# Revit family: HARMANN - INDUFLOW CPC
name_source: partatom
category: Mechanical Equipment
units: mm (PartAtom-declared; Revit-internal decimal feet)

## family parameters
Always vertical = No
Cut with Voids When Loaded = No
Maintain Annotation Orientation = No
OmniClass Number = 23.75.00.00
OmniClass Title = Climate Control (HVAC)
Part Type = Normal
Room Calculation Point = No
Round Connector Dimension = Use Diameter
Shared = No
Work Plane-Based = No

## types (4) — shared parameters
Autor = https://www.archispace.com
Description = Indukcyjny wentylator bytowy
G = 285 mm  [stored 0.935039 ft]
H = 15 mm  [stored 0.0492126 ft]
Ilość faz = 3
Lookup Table Name = INDUFLOW_CPC
Manufacturer = Harmann Polska Sp. z o.o.
Temperatura maksymalna Tmax = 60 °C
Wyłącznik serwisowy = AS
Zasilanie Częstotliwość Nominalna = 50 Hz
Zasilanie napięcie nominalne Unom = 400 V
d = 77 mm  [stored 0.252625 ft]
e = 15 mm  [stored 0.0492126 ft]
h = 70 mm  [stored 0.229659 ft]
zero-valued in all types: Default Elevation

## per-type parameters (varying)
- INDUFLOW CPC 500 D4: A=1446 mm  [stored 4.74409 ft]; B=273 mm  [stored 0.895669 ft]; C=870 mm  [stored 2.85433 ft]; Ciśnienie akustyczne nominalne I bieg Lpa=76.0 dB(A); Ciśnienie akustyczne nominalne II bieg Lpa=-; E=950 mm  [stored 3.1168 ft]; F=243 mm  [stored 0.797244 ft]; K=914 mm  [stored 2.99869 ft]; Masa=56.00 kg; N1=1 mm; Numer artykułu=15957800; Obroty maksymalne I bieg nmax=0.000 RPM; Obroty maksymalne II bieg nmax=1450.000 RPM; Powietrze Przepływ Maksymalny I Qmax=0 m³/h; Powietrze Przepływ Maksymalny II Qmax=6530 m³/h; Siła ciągu I bieg F=0.00 N; Siła ciągu II bieg F=51.00 N; Typ=Jednobiegowy; Zasilanie Moc maksymalna I Pmax=0 W; Zasilanie Moc maksymalna II Pmax=1891 W; Zasilanie Rodzaj Sterowania=I bieg Y; Zasilanie natężenie maksymalne I bieg Imax=4 A; Zasilanie natężenie maksymalne II bieg Imax=0 A; a=110 mm  [stored 0.360892 ft]; b=228.5 mm  [stored 0.749672 ft]; c=714 mm  [stored 2.34252 ft]; f=163 mm  [stored 0.534777 ft]; g=163 mm  [stored 0.534777 ft]
- INDUFLOW CPC 500 D84: A=1446 mm  [stored 4.74409 ft]; B=273 mm  [stored 0.895669 ft]; C=870 mm  [stored 2.85433 ft]; Ciśnienie akustyczne nominalne I bieg Lpa=61.0 dB(A); Ciśnienie akustyczne nominalne II bieg Lpa=76.0 dB(A); E=950 mm  [stored 3.1168 ft]; F=243 mm  [stored 0.797244 ft]; K=914 mm  [stored 2.99869 ft]; Masa=56.00 kg; N1=2 mm; Numer artykułu=15962200; Obroty maksymalne I bieg nmax=700.000 RPM; Obroty maksymalne II bieg nmax=1460.000 RPM; Powietrze Przepływ Maksymalny I Qmax=3300 m³/h; Powietrze Przepływ Maksymalny II Qmax=6530 m³/h; Siła ciągu I bieg F=12.00 N; Siła ciągu II bieg F=50.00 N; Typ=Dwubiegowy; Zasilanie Moc maksymalna I Pmax=350 W; Zasilanie Moc maksymalna II Pmax=2094 W; Zasilanie Rodzaj Sterowania=II biegi Y/YY; Zasilanie natężenie maksymalne I bieg Imax=5 A; Zasilanie natężenie maksymalne II bieg Imax=2 A; a=110 mm  [stored 0.360892 ft]; b=228.5 mm  [stored 0.749672 ft]; c=714 mm  [stored 2.34252 ft]; f=163 mm  [stored 0.534777 ft]; g=163 mm  [stored 0.534777 ft]
- INDUFLOW CPC 560 D4: A=1753 mm  [stored 5.75131 ft]; B=301 mm  [stored 0.987533 ft]; C=974 mm  [stored 3.19554 ft]; Ciśnienie akustyczne nominalne I bieg Lpa=0.0 dB(A); Ciśnienie akustyczne nominalne II bieg Lpa=77.0 dB(A); E=1054 mm  [stored 3.45801 ft]; F=271 mm  [stored 0.889108 ft]; K=1020 mm  [stored 3.34646 ft]; Masa=73.00 kg; N1=3 mm; Numer artykułu=15769800; Obroty maksymalne I bieg nmax=0.000 RPM; Obroty maksymalne II bieg nmax=1440.000 RPM; Powietrze Przepływ Maksymalny I Qmax=0 m³/h; Powietrze Przepływ Maksymalny II Qmax=7920 m³/h; Siła ciągu I bieg F=0.00 N; Siła ciągu II bieg F=80.00 N; Typ=Jednobiegowy; Zasilanie Moc maksymalna I Pmax=0 W; Zasilanie Moc maksymalna II Pmax=2692 W; Zasilanie Rodzaj Sterowania=I bieg Y; Zasilanie natężenie maksymalne I bieg Imax=0 A; Zasilanie natężenie maksymalne II bieg Imax=5 A; a=164.5 mm  [stored 0.539698 ft]; b=281.5 mm  [stored 0.923556 ft]; c=814 mm  [stored 2.6706 ft]; f=187.5 mm  [stored 0.615157 ft]; g=181 mm  [stored 0.593832 ft]
- INDUFLOW CPC 560 D84: A=1753 mm  [stored 5.75131 ft]; B=301 mm  [stored 0.987533 ft]; C=974 mm  [stored 3.19554 ft]; Ciśnienie akustyczne nominalne I bieg Lpa=61.0 dB(A); Ciśnienie akustyczne nominalne II bieg Lpa=77.0 dB(A); E=1054 mm  [stored 3.45801 ft]; F=271 mm  [stored 0.889108 ft]; K=1020 mm  [stored 3.34646 ft]; Masa=71.00 kg; N1=4 mm; Numer artykułu=15967200; Obroty maksymalne I bieg nmax=1440.000 RPM; Obroty maksymalne II bieg nmax=1460.000 RPM; Powietrze Przepływ Maksymalny I Qmax=3990 m³/h; Powietrze Przepływ Maksymalny II Qmax=7980 m³/h; Siła ciągu I bieg F=20.00 N; Siła ciągu II bieg F=81.00 N; Typ=Dwubiegowy; Zasilanie Moc maksymalna I Pmax=597 W; Zasilanie Moc maksymalna II Pmax=3060 W; Zasilanie Rodzaj Sterowania=II biegi Y/YY; Zasilanie natężenie maksymalne I bieg Imax=2 A; Zasilanie natężenie maksymalne II bieg Imax=6 A; a=164.5 mm  [stored 0.539698 ft]; b=281.5 mm  [stored 0.923556 ft]; c=814 mm  [stored 2.6706 ft]; f=187.5 mm  [stored 0.615157 ft]; g=181 mm  [stored 0.593832 ft]

note: column(s) folded — value = type name in every type: Model

note: [stored X ft] marks values corroborated as IEEE doubles in the binary element streams (Revit-internal decimal feet)

## geometry (parser evidence)
native form markers: Sweep x2
no freeform markers — native parametric forms only
